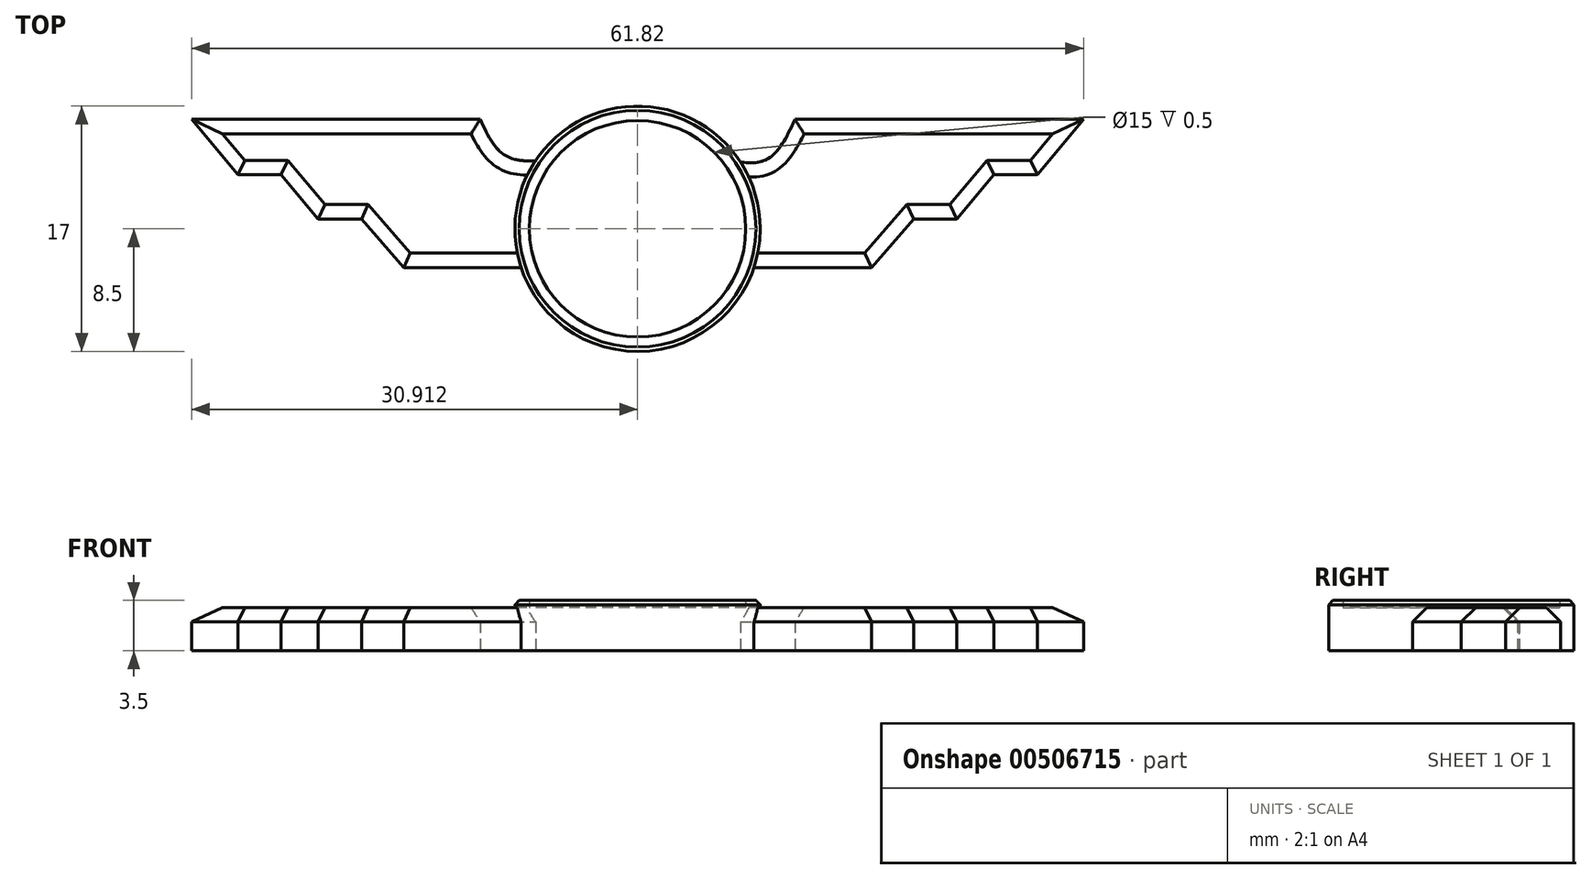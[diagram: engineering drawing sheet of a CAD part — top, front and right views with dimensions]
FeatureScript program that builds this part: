
annotation { "Feature Type Name" : "Feature", "Feature Type Description" : "" }
export const myFeature = defineFeature(function(context is Context, id is Id, definition is map)
    precondition{}
    {
        {
            var Q0;
            Q0=qCreatedBy(makeId("Top.planeOp"),FACE);
            var sketch = newSketch(context, id + "F0", { "sketchPlane" : qUnion([Q0])});
            skCircle(sketch, "E0", {"center": v(-4.55, 0) * mm, "radius": 7.5 * mm});
            skCircle(sketch, "E1", {"center": v(-4.55, 0) * mm, "radius": 8.5 * mm});
            skPoint(sketch, "E2", {"position": v(1.18, 4.84) * mm});
            skPoint(sketch, "E3", {"position": v(-9.55, 5) * mm});
            skFitSpline(sketch, "E4", {"points": [v(1.18, 4.84) * mm, v(4.47, 4.84) * mm, v(6.36, 7.58) * mm], "startDerivative": vector(8.56, -1.45) * mm, "endDerivative": vector(3.16, 6.76) * mm});
            skLineSegment(sketch, "E5", {"start": v(6.36, 7.58) * mm, "end": v(26.36, 7.58) * mm});
            skLineSegment(sketch, "E6", {"start": v(26.36, 7.58) * mm, "end": v(23.15, 3.75) * mm});
            skLineSegment(sketch, "E7", {"start": v(23.15, 3.75) * mm, "end": v(9.15, 3.75) * mm});
            skPoint(sketch, "E8", {"position": v(20.15, 3.75) * mm});
            skLineSegment(sketch, "E9", {"start": v(20.15, 3.75) * mm, "end": v(17.57, 0.69) * mm});
            skLineSegment(sketch, "E10", {"start": v(17.57, 0.69) * mm, "end": v(6.57, 0.69) * mm});
            skPoint(sketch, "E11", {"position": v(14.57, 0.69) * mm});
            skLineSegment(sketch, "E12", {"start": v(14.57, 0.69) * mm, "end": v(11.66, -2.69) * mm});
            skLineSegment(sketch, "E13", {"start": v(11.66, -2.69) * mm, "end": v(3.52, -2.69) * mm});
            skLineSegment(sketch, "E14.MirrorCS", {"start": v(-29.24, 3.75) * mm, "end": v(-26.67, 0.69) * mm});
            skLineSegment(sketch, "E15.MirrorCS", {"start": v(-32.24, 3.75) * mm, "end": v(-18.24, 3.75) * mm});
            skPoint(sketch, "E16.MirrorP", {"position": v(-23.67, 0.69) * mm});
            skLineSegment(sketch, "E17.MirrorCS", {"start": v(-26.67, 0.69) * mm, "end": v(-15.67, 0.69) * mm});
            skLineSegment(sketch, "E18.MirrorCS", {"start": v(-23.67, 0.69) * mm, "end": v(-20.75, -2.69) * mm});
            skPoint(sketch, "E19.MirrorP", {"position": v(-29.24, 3.75) * mm});
            skLineSegment(sketch, "E20.MirrorCS", {"start": v(-35.46, 7.58) * mm, "end": v(-32.24, 3.75) * mm});
            skLineSegment(sketch, "E21.MirrorCS", {"start": v(-15.46, 7.58) * mm, "end": v(-35.46, 7.58) * mm});
            skFitSpline(sketch, "E22.MirrorCS", {"points": [v(-9.55, 5) * mm, v(-13.57, 5) * mm, v(-15.46, 7.58) * mm], "startDerivative": vector(-8.56, -1.45) * mm, "endDerivative": vector(-3.16, 6.76) * mm});
            skLineSegment(sketch, "E23.MirrorCS", {"start": v(-20.75, -2.69) * mm, "end": v(-12.61, -2.69) * mm});
            skSolve(sketch);
        }
        {
            var Q0;
            {var subQ1=sQuery(id+"F0.wireOp",EDGE,"E5");Q0=makeQuery(id+"F0.imprint","IMPRINT",FACE,{"disambiguationData":[TD([[makeQuery(id+"F0.imprint","IMPRINT",EDGE,{"derivedFrom":subQ1}),-1.0]])]});}
            var Q1;
            {var subQ2=sQuery(id+"F0.wireOp",EDGE,"E4");var subQ7=sQuery(id+"F0.wireOp",EDGE,"E0");var subQ8=makeQuery(id+"F0.imprint","INTERSECT",VERTEX,{"derivedFrom":[subQ7,subQ2]});Q1=makeQuery(id+"F0.imprint","IMPRINT",FACE,{"disambiguationData":[TD([[makeQuery(id+"F0.imprint","IMPRINT",EDGE,{"disambiguationData":[TD([[subQ8,1.0]])],"derivedFrom":subQ7}),-1.0]])]});}
            var Q2;
            {var subQ0=sQuery(id+"F0.wireOp",EDGE,"E4");var subQ1=sQuery(id+"F0.wireOp",EDGE,"E0");var subQ2=makeQuery(id+"F0.imprint","INTERSECT",VERTEX,{"derivedFrom":[subQ1,subQ0]});Q2=makeQuery(id+"F0.imprint","IMPRINT",FACE,{"disambiguationData":[TD([[makeQuery(id+"F0.imprint","IMPRINT",EDGE,{"disambiguationData":[TD([[subQ2,-1.0]])],"derivedFrom":subQ1}),-1.0]])]});}
            var Q3;
            {var subQ0=sQuery(id+"F0.wireOp",EDGE,"E0");var subQ1=makeQuery(id+"F0.imprint","INTERSECT",VERTEX,{"derivedFrom":[subQ0,sQuery(id+"F0.wireOp",EDGE,"E4")]});Q3=makeQuery(id+"F0.imprint","IMPRINT",FACE,{"disambiguationData":[TD([[makeQuery(id+"F0.imprint","IMPRINT",EDGE,{"disambiguationData":[TD([[subQ1,-1.0]])],"derivedFrom":subQ0}),1.0]])]});}
            var Q4;
            {var subQ1=sQuery(id+"F0.wireOp",EDGE,"E14.MirrorCS");Q4=makeQuery(id+"F0.imprint","IMPRINT",FACE,{"disambiguationData":[TD([[makeQuery(id+"F0.imprint","IMPRINT",EDGE,{"derivedFrom":subQ1}),1.0]])]});}
            extrude(context, id + "F1", {"entities" : qUnion([Q0, Q1, Q2, Q3, Q4]), "depth" : 3 * mm});
        }
        {
            var Q0;
            {var subQ2=sQuery(id+"F0.wireOp",EDGE,"E4");var subQ7=sQuery(id+"F0.wireOp",EDGE,"E0");var subQ8=makeQuery(id+"F0.imprint","INTERSECT",VERTEX,{"derivedFrom":[subQ7,subQ2]});Q0=makeQuery(id+"F0.imprint","IMPRINT",FACE,{"disambiguationData":[TD([[makeQuery(id+"F0.imprint","IMPRINT",EDGE,{"disambiguationData":[TD([[subQ8,1.0]])],"derivedFrom":subQ7}),-1.0]])]});}
            var Q1;
            {var subQ0=sQuery(id+"F0.wireOp",EDGE,"E4");var subQ1=sQuery(id+"F0.wireOp",EDGE,"E0");var subQ2=makeQuery(id+"F0.imprint","INTERSECT",VERTEX,{"derivedFrom":[subQ1,subQ0]});Q1=makeQuery(id+"F0.imprint","IMPRINT",FACE,{"disambiguationData":[TD([[makeQuery(id+"F0.imprint","IMPRINT",EDGE,{"disambiguationData":[TD([[subQ2,-1.0]])],"derivedFrom":subQ1}),-1.0]])]});}
            extrude(context, id + "F2", {"entities" : qUnion([Q0, Q1]), "operationType" : NewBodyOperationType.ADD, "depth" : 3.5 * mm});
        }
        {
            var Q0;
            Q0=makeQuery(id+"F1.opExtrude","CAP_EDGE",EDGE,{"disambiguationData":[OSD([sQuery(id+"F0.wireOp",EDGE,"E20.MirrorCS")])],"isStart":false});
            var Q1;
            Q1=makeQuery(id+"F1.opExtrude","CAP_EDGE",EDGE,{"disambiguationData":[OSD([sQuery(id+"F0.wireOp",EDGE,"E15.MirrorCS")])],"isStart":false});
            var Q2;
            Q2=makeQuery(id+"F1.opExtrude","CAP_EDGE",EDGE,{"disambiguationData":[OSD([sQuery(id+"F0.wireOp",EDGE,"E14.MirrorCS")])],"isStart":false});
            var Q3;
            Q3=makeQuery(id+"F1.opExtrude","CAP_EDGE",EDGE,{"disambiguationData":[OSD([sQuery(id+"F0.wireOp",EDGE,"E17.MirrorCS")])],"isStart":false});
            var Q4;
            Q4=makeQuery(id+"F1.opExtrude","CAP_EDGE",EDGE,{"disambiguationData":[OSD([sQuery(id+"F0.wireOp",EDGE,"E18.MirrorCS")])],"isStart":false});
            chamfer(context, id + "F3", {"entities" : qUnion([Q0, Q1, Q2, Q3, Q4]), "width" : 1 * mm, "tangentPropagation" : true});
        }
        {
            var Q0;
            Q0=makeQuery(id+"F1.opExtrude","CAP_EDGE",EDGE,{"disambiguationData":[OSD([sQuery(id+"F0.wireOp",EDGE,"E6")])],"isStart":false});
            var Q1;
            Q1=makeQuery(id+"F1.opExtrude","CAP_EDGE",EDGE,{"disambiguationData":[OSD([sQuery(id+"F0.wireOp",EDGE,"E7")])],"isStart":false});
            var Q2;
            Q2=makeQuery(id+"F1.opExtrude","CAP_EDGE",EDGE,{"disambiguationData":[OSD([sQuery(id+"F0.wireOp",EDGE,"E9")])],"isStart":false});
            var Q3;
            Q3=makeQuery(id+"F1.opExtrude","CAP_EDGE",EDGE,{"disambiguationData":[OSD([sQuery(id+"F0.wireOp",EDGE,"E10")])],"isStart":false});
            var Q4;
            Q4=makeQuery(id+"F1.opExtrude","CAP_EDGE",EDGE,{"disambiguationData":[OSD([sQuery(id+"F0.wireOp",EDGE,"E12")])],"isStart":false});
            chamfer(context, id + "F4", {"entities" : qUnion([Q0, Q1, Q2, Q3, Q4]), "width" : 1 * mm, "tangentPropagation" : true});
        }
        {
            var Q0;
            Q0=makeQuery(id+"F1.opExtrude","CAP_EDGE",EDGE,{"disambiguationData":[OSD([sQuery(id+"F0.wireOp",EDGE,"E23.MirrorCS")])],"isStart":false});
            var Q1;
            Q1=makeQuery(id+"F1.opExtrude","CAP_EDGE",EDGE,{"disambiguationData":[OSD([sQuery(id+"F0.wireOp",EDGE,"E13")])],"isStart":false});
            chamfer(context, id + "F5", {"entities" : qUnion([Q0, Q1]), "width" : 1 * mm, "tangentPropagation" : true});
        }
        {
            var Q0;
            Q0=makeQuery(id+"F1.opExtrude","CAP_EDGE",EDGE,{"disambiguationData":[OSD([sQuery(id+"F0.wireOp",EDGE,"E4")])],"isStart":false});
            chamfer(context, id + "F6", {"entities" : qUnion([Q0]), "width" : 1 * mm, "tangentPropagation" : true});
        }
        {
            var Q0;
            Q0=makeQuery(id+"F1.opExtrude","CAP_EDGE",EDGE,{"disambiguationData":[OSD([sQuery(id+"F0.wireOp",EDGE,"E5")])],"isStart":false});
            chamfer(context, id + "F7", {"entities" : qUnion([Q0]), "width" : 1 * mm, "tangentPropagation" : true});
        }
        {
            var Q0;
            Q0=makeQuery(id+"F1.opExtrude","CAP_EDGE",EDGE,{"disambiguationData":[OSD([sQuery(id+"F0.wireOp",EDGE,"E21.MirrorCS")])],"isStart":false});
            var Q1;
            Q1=makeQuery(id+"F1.opExtrude","CAP_EDGE",EDGE,{"disambiguationData":[OSD([sQuery(id+"F0.wireOp",EDGE,"E22.MirrorCS")])],"isStart":false});
            chamfer(context, id + "F8", {"entities" : qUnion([Q0, Q1]), "width" : 1 * mm, "tangentPropagation" : true});
        }
        {
            var Q0;
            Q0=makeQuery(id+"F2.opExtrude","CAP_EDGE",EDGE,{"disambiguationData":[OSD([sQuery(id+"F0.wireOp",EDGE,"E1")])],"isStart":false});
            chamfer(context, id + "F9", {"entities" : qUnion([Q0]), "width" : 0.3 * mm, "tangentPropagation" : true});
        }
    });
